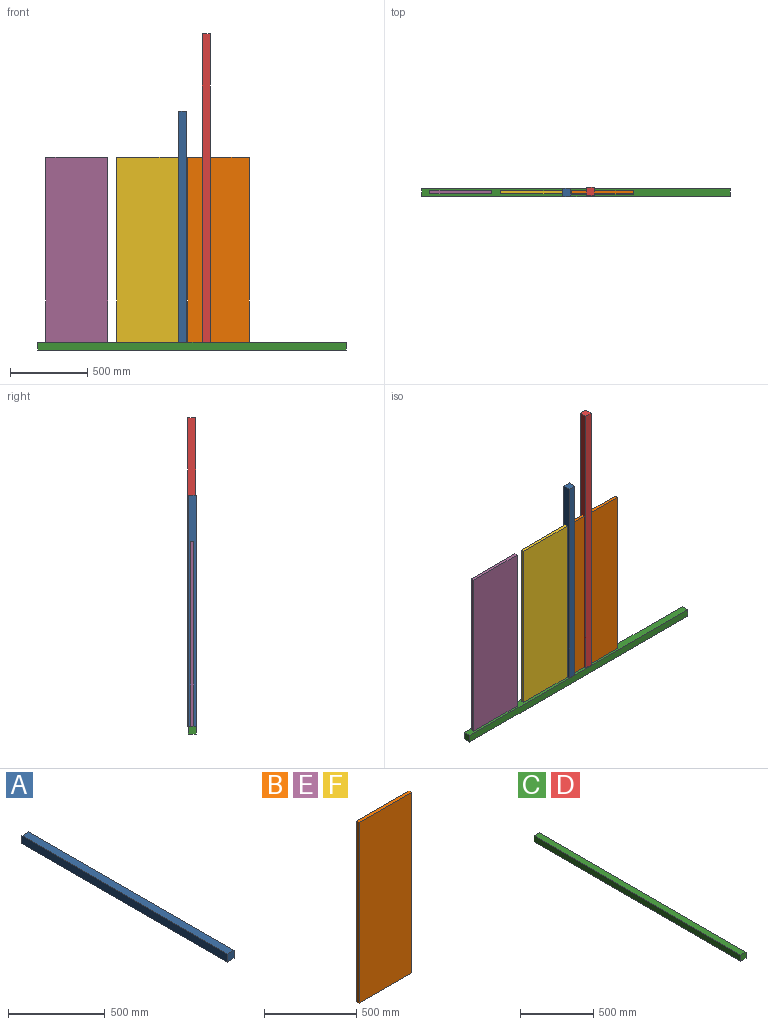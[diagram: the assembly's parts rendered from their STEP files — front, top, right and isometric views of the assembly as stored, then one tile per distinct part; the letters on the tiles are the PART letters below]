
ASSEMBLY  parts=6 mates=6
PART A: 6 faces, bbox 50.8x1500x50.8 mm
  f0: plane 1500x50.8mm, normal (0,0,1), area 76200mm2, adj f1,f3,f4,f5
  f1: plane 1500x50.8mm, normal (-1,0,0), area 76200mm2, adj f0,f2,f4,f5
  f2: plane 1500x50.8mm, normal (0,0,-1), area 76200mm2, adj f1,f3,f4,f5
  f3: plane 1500x50.8mm, normal (1,0,0), area 76200mm2, adj f0,f2,f4,f5
  f4: plane 50.8x50.8mm, normal (0,-1,0), area 2580.6mm2, adj f0,f1,f2,f3
  f5: plane 50.8x50.8mm, normal (0,1,0), area 2580.6mm2, adj f0,f1,f2,f3
PART B: 6 faces, bbox 400x20x1200 mm
  f0: plane 400x20mm, normal (0,0,1), area 8000mm2, adj f1,f3,f4,f5
  f1: plane 1200x20mm, normal (-1,0,0), area 24000mm2, adj f0,f2,f4,f5
  f2: plane 400x20mm, normal (0,0,-1), area 8000mm2, adj f1,f3,f4,f5
  f3: plane 1200x20mm, normal (1,0,0), area 24000mm2, adj f0,f2,f4,f5
  f4: plane 1200x400mm, normal (0,-1,0), area 480000mm2, adj f0,f1,f2,f3
  f5: plane 1200x400mm, normal (0,1,0), area 480000mm2, adj f0,f1,f2,f3
PART C: 6 faces, bbox 50.8x2000x50.8 mm
  f0: plane 2000x50.8mm, normal (0,0,1), area 101600mm2, adj f1,f3,f4,f5
  f1: plane 2000x50.8mm, normal (-1,0,0), area 101600mm2, adj f0,f2,f4,f5
  f2: plane 2000x50.8mm, normal (0,0,-1), area 101600mm2, adj f1,f3,f4,f5
  f3: plane 2000x50.8mm, normal (1,0,0), area 101600mm2, adj f0,f2,f4,f5
  f4: plane 50.8x50.8mm, normal (0,-1,0), area 2580.6mm2, adj f0,f1,f2,f3
  f5: plane 50.8x50.8mm, normal (0,1,0), area 2580.6mm2, adj f0,f1,f2,f3
PART D: same geometry as C
PART E: same geometry as B
PART F: same geometry as B
PLACE A rot(axis=(1,0,0),90deg) t=(505.14,-189.4,1052.46)mm
PLACE B t=(737.21,-178.41,152.46)mm
PLACE C rot(axis=(-0.58,-0.58,-0.58),120deg) t=(1566.16,-189.4,-625.34)mm
PLACE D rot(axis=(1,0,0),90deg) t=(507.08,-184.21,1552.46)mm
PLACE E t=(-181.75,-177.16,152.46)mm
PLACE F t=(276.6,-177.73,152.46)mm
MATE planar C.f3 <-> E.f2  axis (0,0,1) through (-433.84,-164,-447.54)mm
MATE planar A.f4 <-> C.f3  axis (0,0,-1) through (505.14,-189.4,-447.54)mm
MATE planar D.f4 <-> C.f3  axis (0,0,-1) through (659.48,-184.21,-447.54)mm
MATE planar B.f2 <-> C.f3  axis (0,0,-1) through (737.21,-188.41,-447.54)mm
MATE planar F.f2 <-> C.f3  axis (0,0,-1) through (276.6,-187.73,-447.54)mm
MATE planar A.f0 <-> C.f2  axis (0,-1,0) through (505.14,-214.8,302.46)mm
